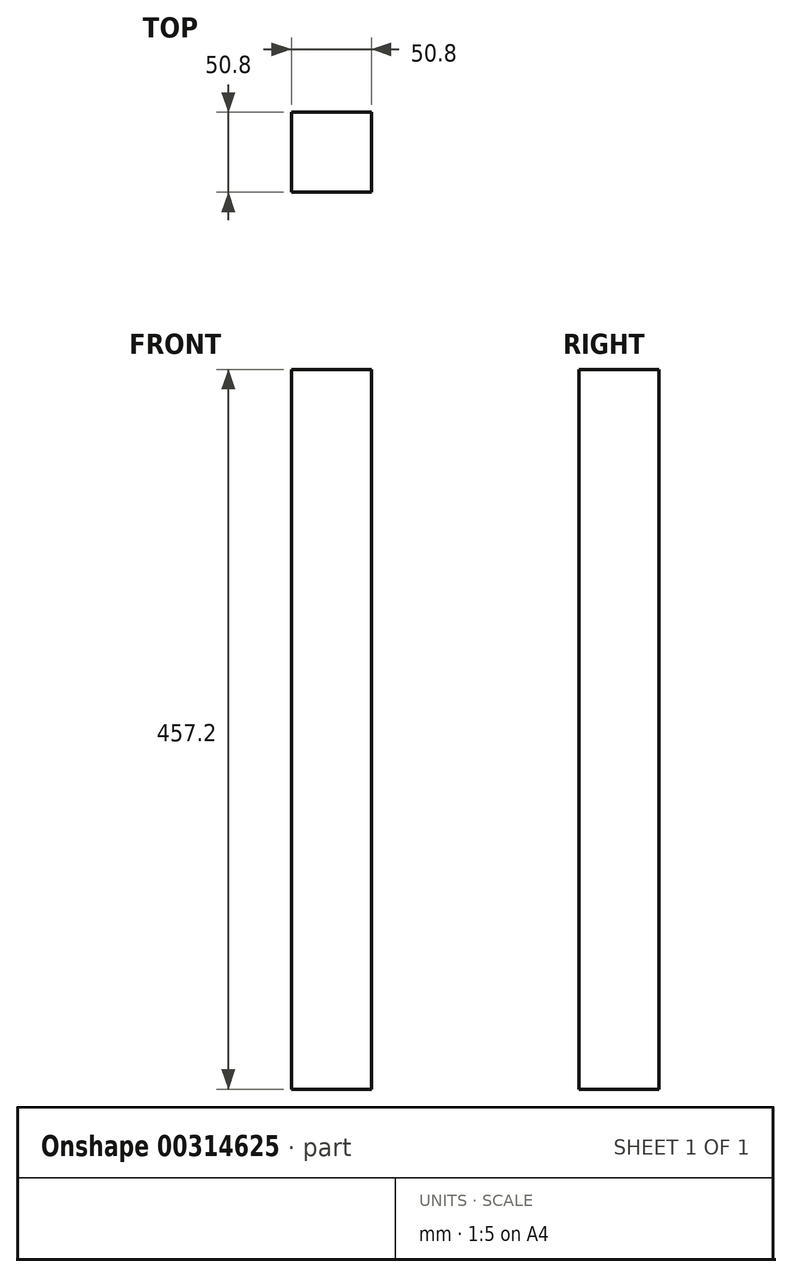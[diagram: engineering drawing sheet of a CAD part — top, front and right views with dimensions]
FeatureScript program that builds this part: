
annotation { "Feature Type Name" : "Feature", "Feature Type Description" : "" }
export const myFeature = defineFeature(function(context is Context, id is Id, definition is map)
    precondition{}
    {
        {
            var Q0;
            Q0=qCreatedBy(makeId("Top.planeOp"),FACE);
            var sketch = newSketch(context, id + "F0", { "sketchPlane" : qUnion([Q0])});
            skLineSegment(sketch, "E0.bottom", {"start": v(25.4, 25.4) * mm, "end": v(-25.4, 25.4) * mm});
            skLineSegment(sketch, "E0.top", {"start": v(25.4, -25.4) * mm, "end": v(-25.4, -25.4) * mm});
            skLineSegment(sketch, "E0.left", {"start": v(25.4, 25.4) * mm, "end": v(25.4, -25.4) * mm});
            skLineSegment(sketch, "E0.right", {"start": v(-25.4, 25.4) * mm, "end": v(-25.4, -25.4) * mm});
            skPoint(sketch, "E0.middle", {"position": v(0, 0) * mm});
            skSolve(sketch);
        }
        {
            var Q0;
            Q0 = qSketchRegion(id + "F0", true);
            extrude(context, id + "F1", {"entities" : qUnion([Q0]), "endBound" : BoundingType.SYMMETRIC, "depth" : 457.2 * mm});
        }
    });
